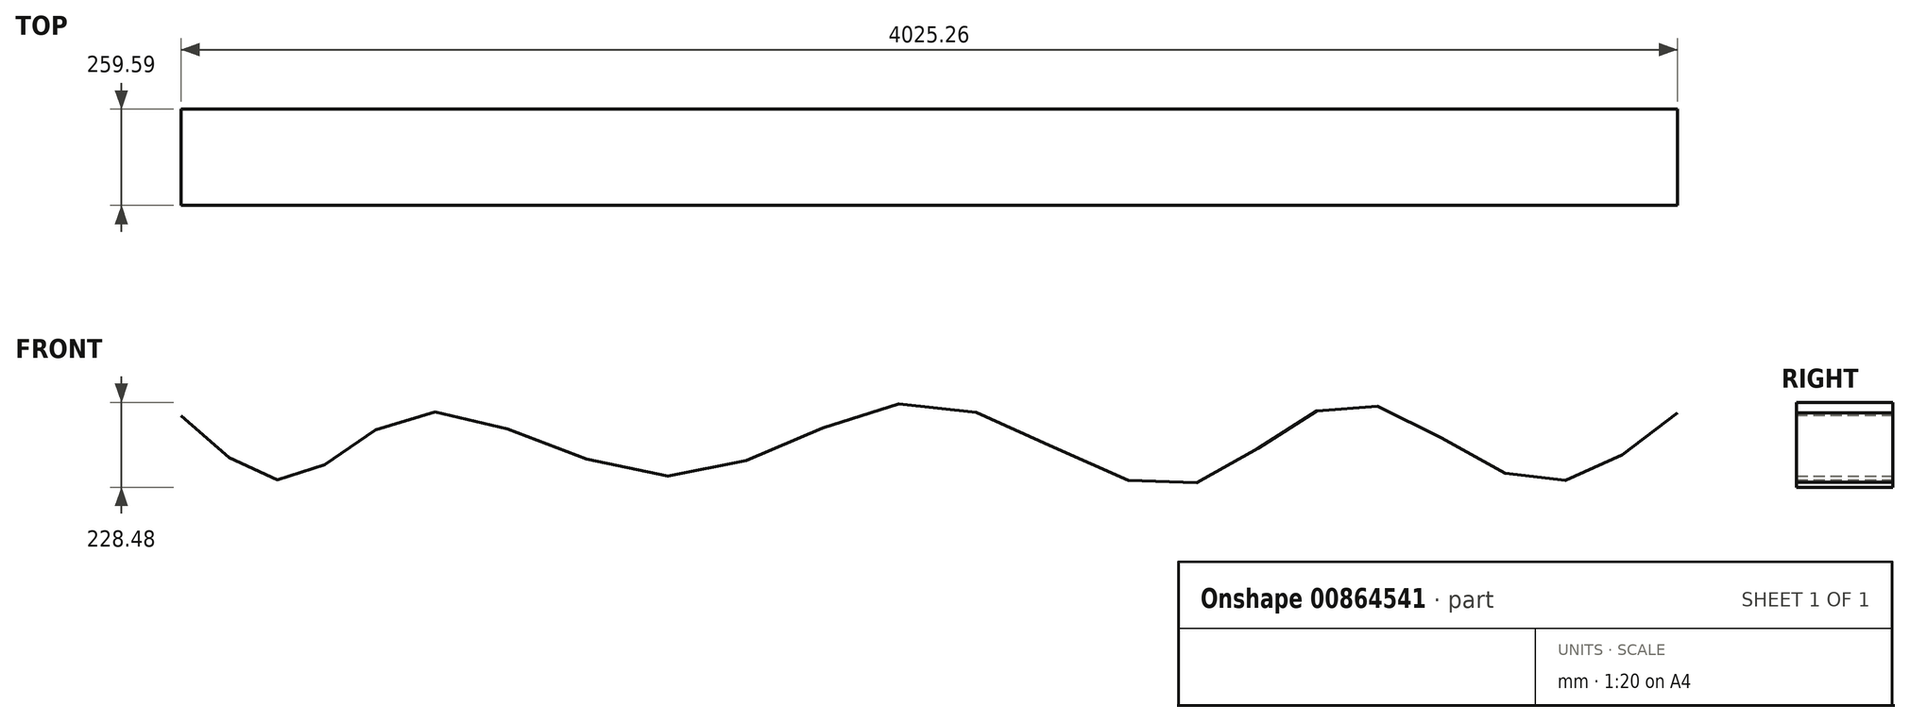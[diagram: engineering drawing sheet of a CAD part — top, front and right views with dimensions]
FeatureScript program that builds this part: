
annotation { "Feature Type Name" : "Feature", "Feature Type Description" : "" }
export const myFeature = defineFeature(function(context is Context, id is Id, definition is map)
    precondition{}
    {
        {
            var Q0;
            Q0=qCreatedBy(makeId("Front.planeOp"),FACE);
            var sketch = newSketch(context, id + "F0", { "sketchPlane" : qUnion([Q0])});
            skLineSegment(sketch, "E0.bottom", {"start": v(-2012.63, 868.75) * mm, "end": v(2012.63, 868.75) * mm, "construction": true});
            skLineSegment(sketch, "E0.top", {"start": v(-2012.63, -868.75) * mm, "end": v(2012.63, -868.75) * mm, "construction": true});
            skLineSegment(sketch, "E0.left", {"start": v(-2012.63, 868.75) * mm, "end": v(-2012.63, -868.75) * mm, "construction": true});
            skLineSegment(sketch, "E0.right", {"start": v(2012.63, 868.75) * mm, "end": v(2012.63, -868.75) * mm, "construction": true});
            skPoint(sketch, "E0.middle", {"position": v(0, 0) * mm});
            skPoint(sketch, "E1", {"position": v(-1369.13, 327.28) * mm});
            skPoint(sketch, "E2", {"position": v(0, 354.7) * mm});
            skPoint(sketch, "E3", {"position": v(1126.2, 354.7) * mm});
            skFitSpline(sketch, "E4", {"points": [v(-2012.63, 319.69) * mm, v(-1712.83, 148.49) * mm, v(-1369.13, 327.28) * mm, v(-689.71, 156.64) * mm, v(0, 354.7) * mm, v(667.65, 128.1) * mm, v(1126.2, 354.7) * mm, v(1613.33, 144.41) * mm, v(2012.63, 327.28) * mm], "startDerivative": vector(3007.42, -2803.76) * mm, "endDerivative": vector(3393.24, 2776.47) * mm});
            skSolve(sketch);
        }
        {
            var Q0;
            Q0=sQuery(id+"F0.wireOp",EDGE,"E0.bottom");
            var Q1;
            Q1=sQuery(id+"F0.wireOp",EDGE,"E0.left");
            var Q2;
            Q2=sQuery(id+"F0.wireOp",EDGE,"E0.top");
            var Q3;
            Q3=sQuery(id+"F0.wireOp",EDGE,"E0.right");
            var Q4;
            Q4=sQuery(id+"F0.wireOp",EDGE,"E4");
            extrude(context, id + "F1", {"bodyType" : ToolBodyType.SURFACE, "surfaceEntities" : qUnion([Q0, Q1, Q2, Q3, Q4]), "depth" : 259.59 * mm, "offsetDistance" : 25.4 * mm});
        }
    });
